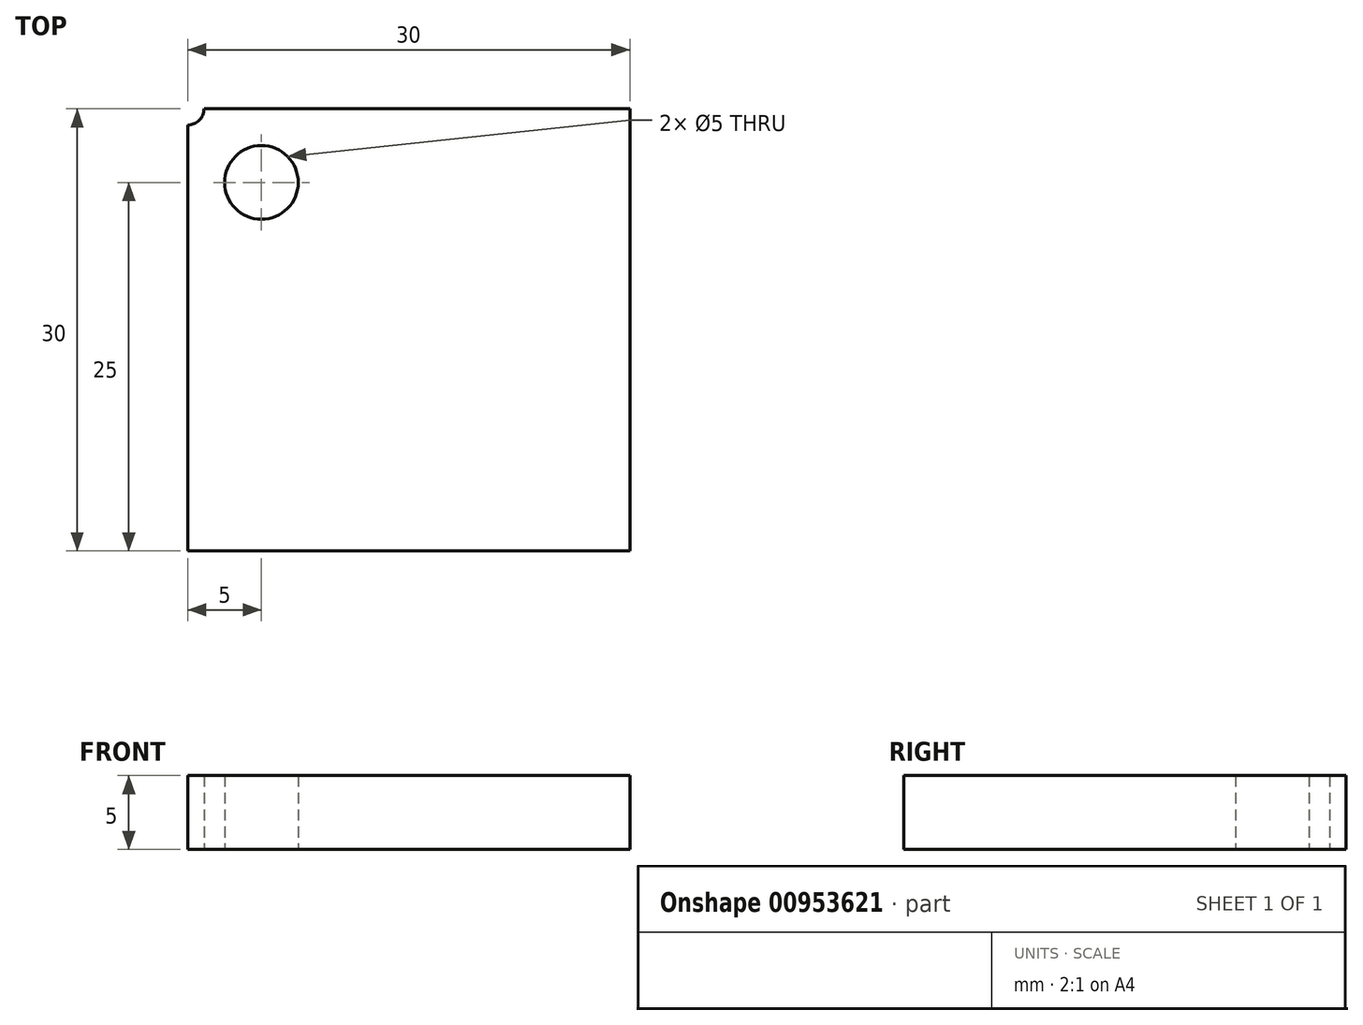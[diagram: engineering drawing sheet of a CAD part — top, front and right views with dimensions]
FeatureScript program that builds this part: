
annotation { "Feature Type Name" : "Feature", "Feature Type Description" : "" }
export const myFeature = defineFeature(function(context is Context, id is Id, definition is map)
    precondition{}
    {
        {
            var Q0;
            Q0=qCreatedBy(makeId("Top.planeOp"),FACE);
            var sketch = newSketch(context, id + "F0", { "sketchPlane" : qUnion([Q0])});
            skLineSegment(sketch, "E0.bottom", {"start": v(0, 0) * mm, "end": v(30, 0) * mm});
            skLineSegment(sketch, "E0.top", {"start": v(0, -30) * mm, "end": v(30, -30) * mm});
            skLineSegment(sketch, "E0.left", {"start": v(0, 0) * mm, "end": v(0, -30) * mm});
            skLineSegment(sketch, "E0.right", {"start": v(30, 0) * mm, "end": v(30, -30) * mm});
            skCircle(sketch, "E1", {"center": v(0, 0) * mm, "radius": 1.1 * mm});
            skCircle(sketch, "E2", {"center": v(5, -5) * mm, "radius": 2.5 * mm});
            skSolve(sketch);
        }
        {
            var Q0;
            {var subQ2=sQuery(id+"F0.wireOp",EDGE,"E0.top");Q0=makeQuery(id+"F0.imprint","IMPRINT",FACE,{"disambiguationData":[TD([[makeQuery(id+"F0.imprint","IMPRINT",EDGE,{"derivedFrom":subQ2}),1.0]])]});}
            extrude(context, id + "F1", {"entities" : qUnion([Q0]), "depth" : 5 * mm, "offsetDistance" : 25 * mm});
        }
    });
